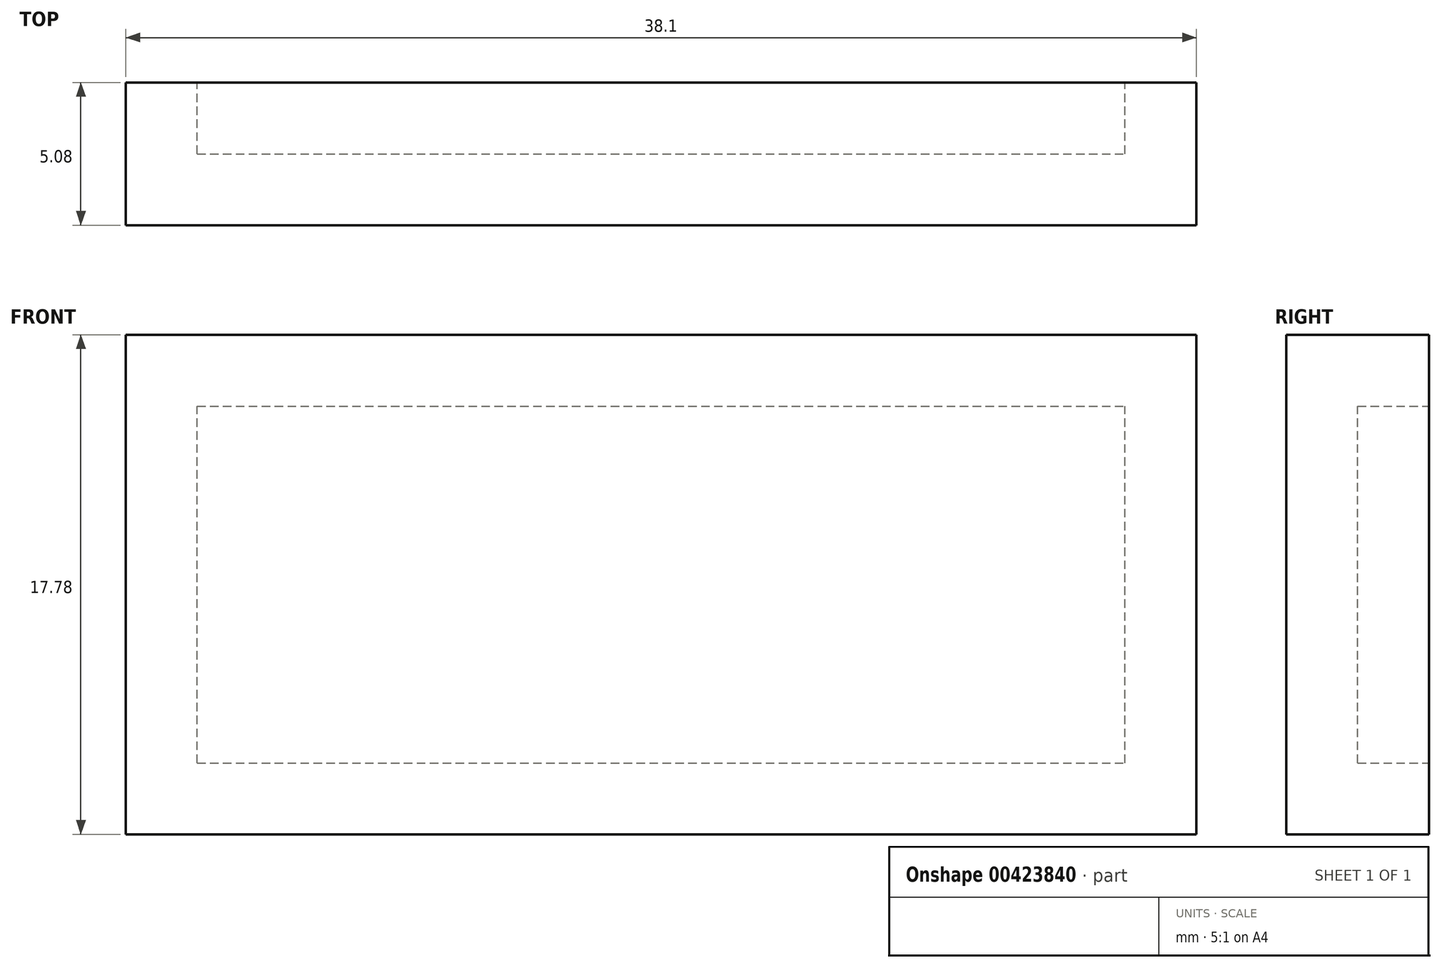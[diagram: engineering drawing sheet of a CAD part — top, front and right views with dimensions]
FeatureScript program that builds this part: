
annotation { "Feature Type Name" : "Feature", "Feature Type Description" : "" }
export const myFeature = defineFeature(function(context is Context, id is Id, definition is map)
    precondition{}
    {
        {
            var Q0;
            Q0=qCreatedBy(makeId("Front.planeOp"),FACE);
            var sketch = newSketch(context, id + "F0", { "sketchPlane" : qUnion([Q0])});
            skLineSegment(sketch, "E0", {"start": v(-18.23, -11.43) * mm, "end": v(19.87, -11.43) * mm});
            skLineSegment(sketch, "E1", {"start": v(19.87, -11.43) * mm, "end": v(19.87, 6.35) * mm});
            skLineSegment(sketch, "E2", {"start": v(-18.23, -11.43) * mm, "end": v(-18.23, 6.35) * mm});
            skLineSegment(sketch, "E3", {"start": v(-18.23, 6.35) * mm, "end": v(19.87, 6.35) * mm});
            skSolve(sketch);
        }
        {
            var Q0;
            Q0=makeQuery(id+"F0.imprint","IMPRINT",FACE,{"disambiguationData":[TD([[makeQuery(id+"F0.imprint","IMPRINT",EDGE,{"derivedFrom":sQuery(id+"F0.wireOp",EDGE,"E0")}),1.0]])]});
            extrude(context, id + "F1", {"entities" : qUnion([Q0]), "depth" : 5.08 * mm});
        }
        {
            var Q0;
            Q0=makeQuery(id+"F1.opExtrude","CAP_FACE",FACE,{"disambiguationData":[OSD([sQuery(id+"F0.wireOp",EDGE,"E0"),sQuery(id+"F0.wireOp",EDGE,"E1"),sQuery(id+"F0.wireOp",EDGE,"E2"),sQuery(id+"F0.wireOp",EDGE,"E3")])],"isStart":true});
            shell(context, id + "F2", {"entities" : qUnion([Q0]), "thickness" : 5.08 * mm});
        }
        {
            var Q0;
            Q0=makeQuery(id+"F1.opExtrude","CAP_FACE",FACE,{"disambiguationData":[OSD([sQuery(id+"F0.wireOp",EDGE,"E0"),sQuery(id+"F0.wireOp",EDGE,"E1"),sQuery(id+"F0.wireOp",EDGE,"E2"),sQuery(id+"F0.wireOp",EDGE,"E3")])],"isStart":true});
            shell(context, id + "F3", {"entities" : qUnion([Q0]), "thickness" : 2.54 * mm});
        }
    });
